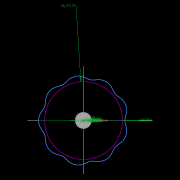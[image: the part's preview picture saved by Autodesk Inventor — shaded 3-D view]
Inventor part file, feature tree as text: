
AUTODESK INVENTOR PART (.ipt)
format: ipt  version: 2022.2 (Build 262287010, 287A)  size: 501,248 bytes
history: native  units: mm
features: other x19, extrude x15, sketch x9, pattern_circular x7, fillet x2, move_body x2, revolve x2, draft x2, plane x2, chamfer x2
ambient origin geometry x8: Origin, YZ Plane, XZ Plane, XY Plane, X Axis, Y Axis, Z Axis, Center Point
bodies: Solid5 (feature_tree)
feature tree (62):
  other  "CrossSection1"
  sketch  "Sketch7"  dims[d90=15.767323mm]
  other  "Roller1"
  other  "Roller2"
  sketch  "Sketch22"  dims[d167=8.972256mm]
  sketch  "Sketch2"  dims[d57=4.025mm]
  sketch  "Sketch23"  dims[d173=10.814812mm]
  other  "RevRoller1"
  fillet  "Fillet1"  Radius=13.336791mm
  pattern_circular  "Circular Pattern13"  Count=360  [1 undecoded]
  move_body  "Move Body7"
  revolve  "Revolution13"  [1 undecoded]
  fillet  "Fillet3"  Radius=0.025mm
  pattern_circular  "Circular Pattern14"  [2 undecoded]
  move_body  "Move Body6"
  revolve  "Revolution14"  [1 undecoded]
  other  "OuterRim_Top2"
  other  "OuterRim_Bottom2"
  extrude  "Rotor_Ring"  Depth=1.0mm
  draft  "FaceDraft2"
  sketch  "Sketch30"  dims[d201=53.5mm d232=0.0mm d233=3600.0mm]
  plane  "Work Plane5"
  other  "Rotor Featurs"
  other  "RotorRim_Bottom"
  extrude  "Extrusion24"  Depth=1.0mm
  extrude  "Extrusion25"  Depth=1.0mm
  extrude  "Extrusion26"  Depth=1.0mm
  pattern_circular  "Circular Pattern23"  [2 undecoded]
  sketch  "Sketch41"  dims[d346=0.025mm]
  extrude  "Extrusion27"  Depth=1.0mm
  extrude  "Extrusion28"  TaperAngle=90.0deg  [1 undecoded]
  pattern_circular  "Circular Pattern24"  [2 undecoded]
  extrude  "Extrusion29"  Depth=1.0mm
  extrude  "Extrusion30"  TaperAngle=360.0deg  [1 undecoded]
  extrude  "Extrusion31"  TaperAngle=30.0deg  [1 undecoded]
  pattern_circular  "Circular Pattern25"  [2 undecoded]
  sketch  "Sketch42"  dims[d347=0.1mm]
  extrude  "Extrusion32"  Depth=1.0mm
  extrude  "Extrusion33"  Depth=1.0mm
  extrude  "Extrusion34"  Depth=1.0mm
  extrude  "Extrusion35"  TaperAngle=30.0deg  [1 undecoded]
  pattern_circular  "Circular Pattern26"  Angle=90.0deg  [1 undecoded]
  pattern_circular  "Circular Pattern27"  [2 undecoded]
  chamfer  "Chamfer1"  Distance=60.0mm
  chamfer  "Chamfer2"  Angle=360.0deg  [1 undecoded]
  draft  "FaceDraft4"
  plane  "Work Plane6"
  sketch  "Sketch43"  dims[d348=0.1mm d349=17.374602mm d350=17.374329mm d351=0.025mm d352=0.025mm d354=0.025mm d355=17.374329mm d356=17.374602mm d357=1.0mm d358=90.0deg d359=0.5mm d360=60.0mm d361=360.0deg d363=30.0deg d367=8.1mm d369=4.014775mm d370=0.025mm d371=1.0mm d372=30.0deg d373=90.0deg d374=0.5mm d375=60.0mm d376=360.0deg d378=90.0deg d379=0.1mm d380=0.025mm d381=0.025mm d382=0.025mm d383=0.025mm d384=10.461905mm d385=0.0mm d386=0.0mm d391=1.0mm d392=53.5mm d393=1.5mm d394=1.5mm d395=1.5mm d396=1.5mm d397=90.0deg d398=90.0deg d399=90.0deg d400=53.5mm d401=10.461905mm d402=0.0mm d486=0.436332mm d487=0.5mm d488=2.0mm d489=0.0mm d490=20.0mm d495=2.5mm d496=8.0mm d506=13.856406mm d507=55.5mm d508=8.0mm d509=0.05mm d510=2.5mm d511=30.0deg d512=12.0mm d513=6.0mm d514=0.2mm d515=30.0deg d516=131.0mm d517=65.5mm d518=0.2mm d519=100.0mm d520=120.0mm d521=2.0mm d522=150.0mm d530=50.0mm d531=5.5mm d532=5.5mm d533=5.5mm d534=85.75mm d535=73.5mm d536=61.25mm d537=24.5mm d538=3.0mm d539=2.4mm d540=0.0mm d541=0.0mm d542=0.0mm d543=5.5mm d544=3.0mm d545=0.0mm d546=90.0mm d547=360.0deg d549=3.0mm d550=3.0mm d551=2.4mm d552=0.0mm d553=5.230953mm d554=0.0mm d555=2.4mm d556=0.0mm d557=5.230953mm d558=0.0mm d559=5.230953mm d560=0.0mm d561=90.0mm d562=360.0deg d564=60.0mm d565=360.0deg d567=5.5mm d568=5.5mm d569=3.0mm d570=0.0mm d571=5.230953mm d572=0.0mm d573=3.0mm d574=0.0mm d575=5.230953mm d576=0.0mm d577=90.0mm d578=360.0deg d580=60.0mm d581=360.0deg d584=20.0mm d585=8.0mm d587=1.75mm d589=3.0mm d592=2.0mm d593=12.0mm d594=12.0mm d600=0.5mm d601=2.0mm d602=45.0deg d603=0.5mm d604=2.0mm d605=45.0deg d606=0.436332mm d607=0.5mm d608=0.0mm d609=20.0mm d611=360.0deg d613=0.0mm d614=0.0mm d16=0.872665mm d17=0.872665mm d49=0.872665mm d50=0.872665mm d51=0.872665mm d52=0.872665mm d236=0.5mm d237=0.872665mm d238=0.5mm d239=0.872665mm d282=1.0mm d283=1.0mm d284=1.0mm d285=0.15mm d286=0.25mm d287=0.375mm d288=14.3117mm d289=0.75mm d290=20.594885mm d291=0.0625mm d292=0.75mm d293=0.375mm d405=0.5mm d406=0.872665mm d407=0.5mm d408=0.872665mm d413=0.5mm d414=0.872665mm d415=0.5mm d416=0.872665mm d417=0.5mm d418=0.872665mm d419=0.5mm d420=0.872665mm d421=0.872665mm d431=0.5mm d432=0.872665mm d433=0.5mm d434=0.872665mm d471=0.5mm d472=0.872665mm d473=0.5mm d474=0.872665mm d497=0.5mm d498=0.872665mm d499=0.5mm d500=0.872665mm d590=0.5mm d591=0.872665mm]
  extrude  "Extrusion37"  TaperAngle=90.0deg  [1 undecoded]
  extrude  "Extrusion38"  Depth=0.1mm
  other  "2D Equation Curve1"
  sketch  "Sketch40"  dims[d343=17.374329mm d344=17.374602mm d345=0.025mm]
  other  "Work Axis6"
  other  "Work Axis7"
  other  "Work Axis8"
  other  "Work Axis9"
  other  "Work Axis10"
  other  "Work Point1"
  other  "Work Point2"
  other  "Work Point3"
  other  "Work Point4"
  other  "Work Point5"
note: 20 required parameter values undecoded (feature->parameter linkage not recoverable at this tier; creation-order binding heuristic only, values carry confidence <= 0.55)